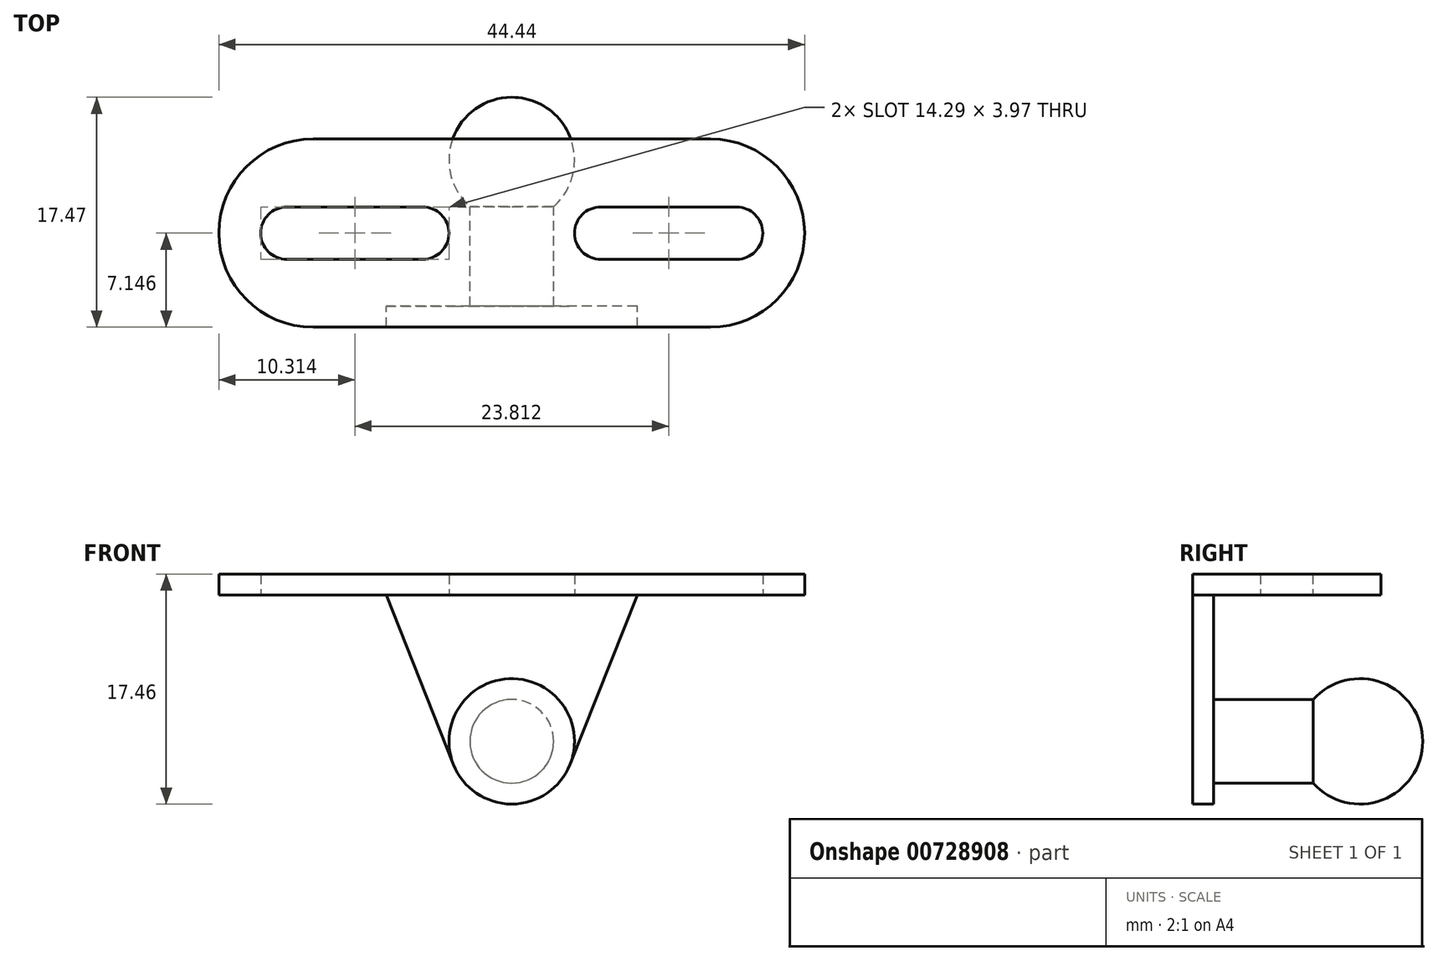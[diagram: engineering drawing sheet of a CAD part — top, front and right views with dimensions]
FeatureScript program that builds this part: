
annotation { "Feature Type Name" : "Feature", "Feature Type Description" : "" }
export const myFeature = defineFeature(function(context is Context, id is Id, definition is map)
    precondition{}
    {
        {
            var Q0;
            Q0=qCreatedBy(makeId("Front.planeOp"),FACE);
            var sketch = newSketch(context, id + "F0", { "sketchPlane" : qUnion([Q0])});
            skCircle(sketch, "E0", {"center": v(0, 0) * mm, "radius": 4.76 * mm});
            skLineSegment(sketch, "E1", {"start": v(9.53, 11.11) * mm, "end": v(-9.53, 11.11) * mm});
            skLineSegment(sketch, "E2", {"start": v(-9.53, 11.11) * mm, "end": v(-4.43, -1.75) * mm});
            skLineSegment(sketch, "E3", {"start": v(9.53, 11.11) * mm, "end": v(4.43, -1.75) * mm});
            skSolve(sketch);
        }
        {
            var Q0;
            Q0=makeQuery(id+"F0.imprint","IMPRINT",FACE,{"disambiguationData":[TD([[makeQuery(id+"F0.imprint","IMPRINT",EDGE,{"derivedFrom":sQuery(id+"F0.wireOp",EDGE,"E0")}),1.0]])]});
            var Q1;
            Q1=makeQuery(id+"F0.imprint","IMPRINT",FACE,{"disambiguationData":[TD([[makeQuery(id+"F0.imprint","IMPRINT",EDGE,{"derivedFrom":sQuery(id+"F0.wireOp",EDGE,"E1")}),1.0]])]});
            extrude(context, id + "F1", {"entities" : qUnion([Q0, Q1]), "depth" : 1.59 * mm, "offsetDistance" : 25.4 * mm});
        }
        {
            var Q0;
            Q0=qCreatedBy(makeId("Top.planeOp"),FACE);
            var sketch = newSketch(context, id + "F2", { "sketchPlane" : qUnion([Q0])});
            skLineSegment(sketch, "E4", {"start": v(3.18, 0) * mm, "end": v(3.18, 7.56) * mm});
            skArc(sketch, "E5", {"start": v(0, 6.35) * mm, "mid": v(4.76, 11.11) * mm, "end": v(0, 15.88) * mm});
            skLineSegment(sketch, "E6", {"start": v(0, 11.11) * mm, "end": v(0, 0) * mm});
            skLineSegment(sketch, "E7", {"start": v(0, 0) * mm, "end": v(3.18, 0) * mm});
            skLineSegment(sketch, "E8", {"start": v(0, 11.11) * mm, "end": v(0, 15.88) * mm});
            skPoint(sketch, "E9.orphan", {"position": v(3.18, 11.11) * mm});
            skSolve(sketch);
        }
        {
            var Q0;
            {var subQ0=sQuery(id+"F2.wireOp",EDGE,"E7");Q0=makeQuery(id+"F2.imprint","IMPRINT",FACE,{"disambiguationData":[TD([[makeQuery(id+"F2.imprint","IMPRINT",EDGE,{"derivedFrom":subQ0}),1.0]])]});}
            var Q1;
            {var subQ0=sQuery(id+"F2.wireOp",EDGE,"E5");var subQ1=makeQuery(id+"F2.imprint","INTERSECT",VERTEX,{"derivedFrom":[sQuery(id+"F2.wireOp",EDGE,"E4"),subQ0]});Q1=makeQuery(id+"F2.imprint","IMPRINT",FACE,{"disambiguationData":[TD([[makeQuery(id+"F2.imprint","IMPRINT",EDGE,{"disambiguationData":[TD([[subQ1,1.0]])],"derivedFrom":subQ0}),1.0]])]});}
            var Q2;
            Q2=sQuery(id+"F2.wireOp",EDGE,"E6");
            revolve(context, id + "F3", {"surfaceOperationType" : NewSurfaceOperationType.NEW, "entities" : qUnion([Q0, Q1]), "axis" : qUnion([Q2]), "revolveType" : RevolveType.FULL});
        }
        {
            var Q0;
            Q0=makeQuery(id+"F1.opExtrude","SWEPT_FACE",FACE,{"disambiguationData":[OSD([sQuery(id+"F0.wireOp",EDGE,"E1")])]});
            var sketch = newSketch(context, id + "F4", { "sketchPlane" : qUnion([Q0])});
            skLineSegment(sketch, "E10.bottom", {"start": v(15.08, -1.59) * mm, "end": v(-15.08, -1.59) * mm});
            skLineSegment(sketch, "E10.top", {"start": v(15.08, 12.7) * mm, "end": v(-15.08, 12.7) * mm});
            skPoint(sketch, "E10.middle", {"position": v(0, 5.56) * mm});
            skPoint(sketch, "E10.middle.positionSnap0", {"position": v(0, 0) * mm});
            skPoint(sketch, "E10.cornerSnap0", {"position": v(0, -1.59) * mm});
            skPoint(sketch, "E10.centerSnap0", {"position": v(0, 0) * mm});
            skArc(sketch, "E11", {"start": v(15.08, -1.59) * mm, "mid": v(22.23, 5.56) * mm, "end": v(15.08, 12.7) * mm});
            skArc(sketch, "E12", {"start": v(-15.08, 12.7) * mm, "mid": v(-22.23, 5.56) * mm, "end": v(-15.08, -1.59) * mm});
            skArc(sketch, "E13", {"start": v(-17.07, 7.54) * mm, "mid": v(-19.05, 5.56) * mm, "end": v(-17.07, 3.57) * mm});
            skArc(sketch, "E14", {"start": v(-6.75, 3.57) * mm, "mid": v(-4.76, 5.56) * mm, "end": v(-6.75, 7.54) * mm});
            skLineSegment(sketch, "E15.bottom", {"start": v(-17.07, 7.54) * mm, "end": v(-6.75, 7.54) * mm});
            skLineSegment(sketch, "E15.top", {"start": v(-17.07, 3.57) * mm, "end": v(-6.75, 3.57) * mm});
            skLineSegment(sketch, "E16.MirrorCS", {"start": v(17.07, 3.57) * mm, "end": v(6.75, 3.57) * mm});
            skLineSegment(sketch, "E17.MirrorCS", {"start": v(17.07, 7.54) * mm, "end": v(6.75, 7.54) * mm});
            skArc(sketch, "E18.MirrorCS", {"start": v(6.75, 3.57) * mm, "mid": v(4.76, 5.56) * mm, "end": v(6.75, 7.54) * mm});
            skArc(sketch, "E19.MirrorCS", {"start": v(17.07, 7.54) * mm, "mid": v(19.05, 5.56) * mm, "end": v(17.07, 3.57) * mm});
            skSolve(sketch);
        }
        {
            var Q0;
            Q0=makeQuery(id+"F4.imprint","IMPRINT",FACE,{"disambiguationData":[TD([[makeQuery(id+"F4.imprint","IMPRINT",EDGE,{"derivedFrom":sQuery(id+"F4.wireOp",EDGE,"E10.top")}),1.0]])]});
            var Q1;
            {var subQ1=sQuery(id+"F0.wireOp",EDGE,"E1");Q1=makeQuery(id+"F4.imprint","IMPRINT",FACE,{"disambiguationData":[TD([[makeQuery(id+"F4.imprint","IMPRINT",EDGE,{"derivedFrom":makeQuery(id+"F1.opExtrude","CAP_EDGE",EDGE,{"disambiguationData":[OSD([subQ1])],"isStart":true})}),1.0]])]});}
            extrude(context, id + "F5", {"entities" : qUnion([Q0, Q1]), "depth" : 1.59 * mm, "offsetDistance" : 25.4 * mm});
        }
    });
